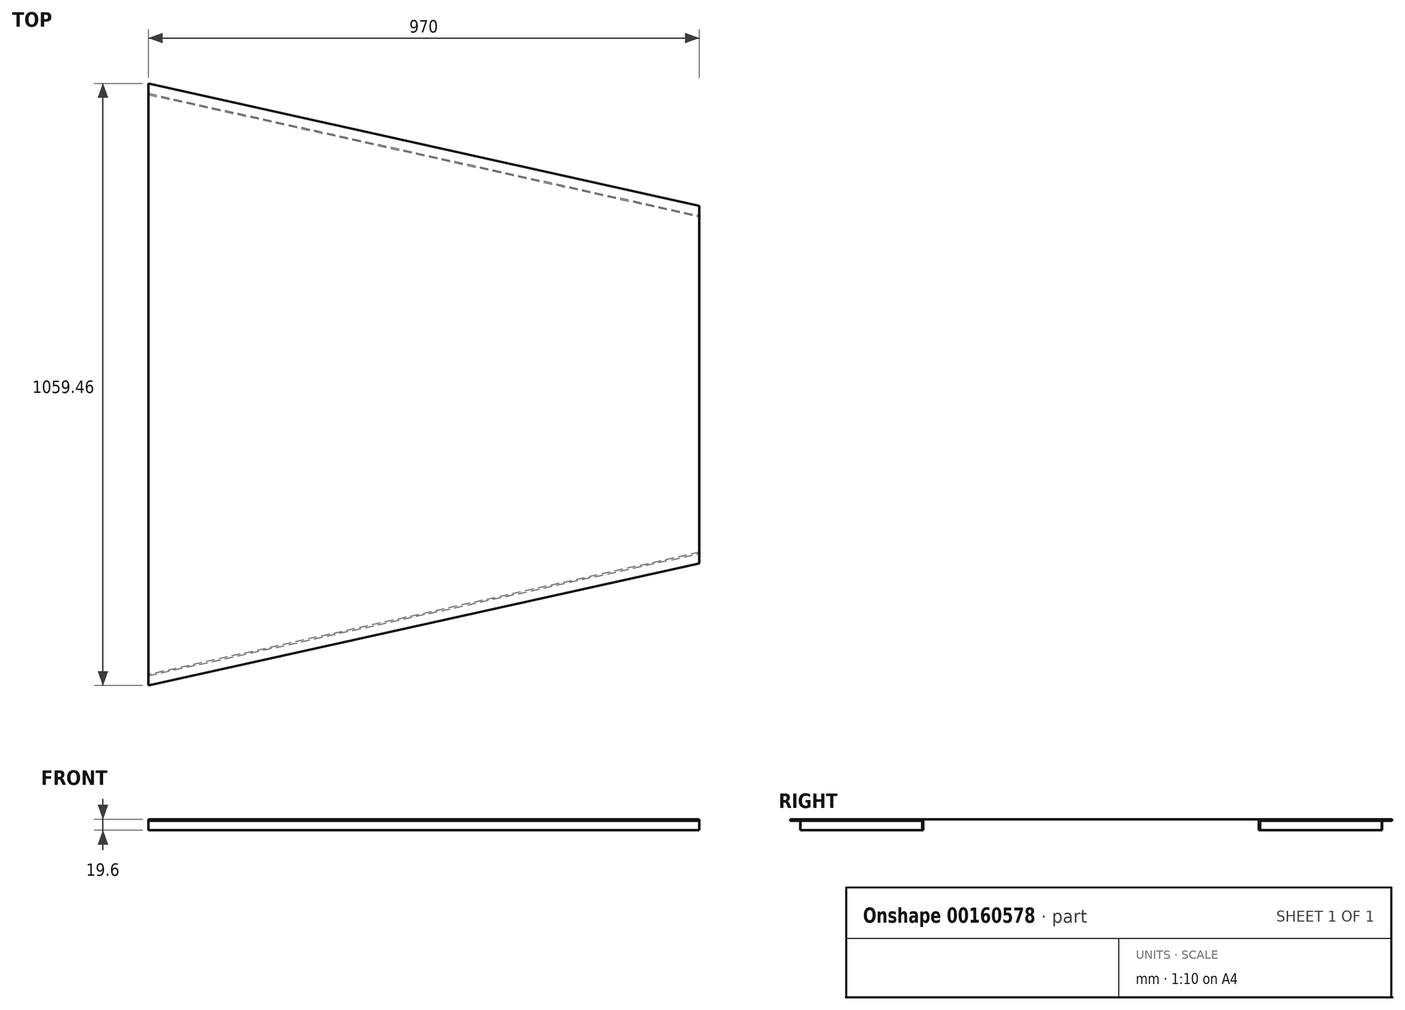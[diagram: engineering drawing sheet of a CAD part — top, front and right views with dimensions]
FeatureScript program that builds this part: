
annotation { "Feature Type Name" : "Feature", "Feature Type Description" : "" }
export const myFeature = defineFeature(function(context is Context, id is Id, definition is map)
    precondition{}
    {
        {
            var Q0;
            Q0=qCreatedBy(makeId("Top.planeOp"),FACE);
            var sketch = newSketch(context, id + "F0", { "sketchPlane" : qUnion([Q0])});
            skLineSegment(sketch, "E0", {"start": v(920.03, 0) * mm, "end": v(920.03, 305) * mm});
            skLineSegment(sketch, "E1", {"start": v(920.03, 305) * mm, "end": v(920.03, -305) * mm});
            skLineSegment(sketch, "E2", {"start": v(-49.97, 0) * mm, "end": v(-49.97, 520) * mm});
            skLineSegment(sketch, "E3", {"start": v(-49.97, 520) * mm, "end": v(920.03, 305) * mm, "construction": true});
            skLineSegment(sketch, "E4", {"start": v(-49.97, -520) * mm, "end": v(-49.97, 520) * mm});
            skLineSegment(sketch, "E5", {"start": v(-49.97, 0) * mm, "end": v(920.03, 0) * mm, "construction": true});
            skLineSegment(sketch, "E6", {"start": v(452.43, 408.64) * mm, "end": v(450.38, 399.37) * mm, "construction": true});
            skLineSegment(sketch, "E7", {"start": v(450.38, 399.37) * mm, "end": v(454.49, 417.92) * mm, "construction": true});
            skLineSegment(sketch, "E8", {"start": v(-49.97, 529.73) * mm, "end": v(-49.97, 520) * mm});
            skLineSegment(sketch, "E9.MirrorCS", {"start": v(-49.97, -529.73) * mm, "end": v(-49.97, -520) * mm});
            skLineSegment(sketch, "E10.MirrorCS", {"start": v(-49.97, -520) * mm, "end": v(920.03, -305) * mm, "construction": true});
            skLineSegment(sketch, "E11", {"start": v(920.03, 305) * mm, "end": v(920.03, 314.73) * mm});
            skLineSegment(sketch, "E12", {"start": v(920.03, 314.73) * mm, "end": v(-49.97, 529.73) * mm});
            skLineSegment(sketch, "E13", {"start": v(920.03, -305) * mm, "end": v(920.03, -314.73) * mm});
            skLineSegment(sketch, "E14", {"start": v(920.03, -314.73) * mm, "end": v(-49.97, -529.73) * mm});
            skLineSegment(sketch, "E15", {"start": v(920.03, -295.27) * mm, "end": v(-49.97, -510.27) * mm});
            skLineSegment(sketch, "E16", {"start": v(-49.97, 510.27) * mm, "end": v(920.03, 295.27) * mm});
            skLineSegment(sketch, "E17", {"start": v(-49.97, -512.32) * mm, "end": v(920.03, -297.32) * mm});
            skLineSegment(sketch, "E18.MirrorCS", {"start": v(-49.97, 512.32) * mm, "end": v(920.03, 297.32) * mm});
            skSolve(sketch);
        }
        {
            var Q0;
            {var subQ0=sQuery(id+"F0.wireOp",EDGE,"E15");Q0=makeQuery(id+"F0.imprint","IMPRINT",FACE,{"disambiguationData":[TD([[makeQuery(id+"F0.imprint","IMPRINT",EDGE,{"derivedFrom":subQ0}),1.0]])]});}
            var Q1;
            {var subQ0=sQuery(id+"F0.wireOp",EDGE,"E16");Q1=makeQuery(id+"F0.imprint","IMPRINT",FACE,{"disambiguationData":[TD([[makeQuery(id+"F0.imprint","IMPRINT",EDGE,{"derivedFrom":subQ0}),1.0]])]});}
            extrude(context, id + "F1", {"entities" : qUnion([Q0, Q1]), "oppositeDirection" : true, "depth" : 19 * mm});
        }
        {
            var Q0;
            {var subQ1=sQuery(id+"F0.wireOp",EDGE,"E8");Q0=makeQuery(id+"F0.imprint","IMPRINT",FACE,{"disambiguationData":[TD([[makeQuery(id+"F0.imprint","IMPRINT",EDGE,{"derivedFrom":subQ1}),1.0]])]});}
            var Q1;
            {var subQ2=sQuery(id+"F0.wireOp",EDGE,"E9.MirrorCS");Q1=makeQuery(id+"F0.imprint","IMPRINT",FACE,{"disambiguationData":[TD([[makeQuery(id+"F0.imprint","IMPRINT",EDGE,{"derivedFrom":subQ2}),-1.0]])]});}
            extrude(context, id + "F2", {"entities" : qUnion([Q0, Q1]), "operationType" : NewBodyOperationType.ADD, "oppositeDirection" : true, "depth" : 2 * mm});
        }
        {
            var Q0;
            {var subQ0=sQuery(id+"F0.wireOp",EDGE,"E15");Q0=makeQuery(id+"F0.imprint","IMPRINT",FACE,{"disambiguationData":[TD([[makeQuery(id+"F0.imprint","IMPRINT",EDGE,{"derivedFrom":subQ0}),-1.0]])]});}
            var Q1;
            {var subQ0=sQuery(id+"F0.wireOp",EDGE,"E15");Q1=makeQuery(id+"F0.imprint","IMPRINT",FACE,{"disambiguationData":[TD([[makeQuery(id+"F0.imprint","IMPRINT",EDGE,{"derivedFrom":subQ0}),1.0]])]});}
            var Q2;
            {var subQ2=sQuery(id+"F0.wireOp",EDGE,"E9.MirrorCS");Q2=makeQuery(id+"F0.imprint","IMPRINT",FACE,{"disambiguationData":[TD([[makeQuery(id+"F0.imprint","IMPRINT",EDGE,{"derivedFrom":subQ2}),-1.0]])]});}
            var Q3;
            {var subQ0=sQuery(id+"F0.wireOp",EDGE,"E16");Q3=makeQuery(id+"F0.imprint","IMPRINT",FACE,{"disambiguationData":[TD([[makeQuery(id+"F0.imprint","IMPRINT",EDGE,{"derivedFrom":subQ0}),1.0]])]});}
            var Q4;
            {var subQ1=sQuery(id+"F0.wireOp",EDGE,"E8");Q4=makeQuery(id+"F0.imprint","IMPRINT",FACE,{"disambiguationData":[TD([[makeQuery(id+"F0.imprint","IMPRINT",EDGE,{"derivedFrom":subQ1}),1.0]])]});}
            extrude(context, id + "F3", {"entities" : qUnion([Q0, Q1, Q2, Q3, Q4]), "operationType" : NewBodyOperationType.ADD, "depth" : .6 * mm});
        }
    });
